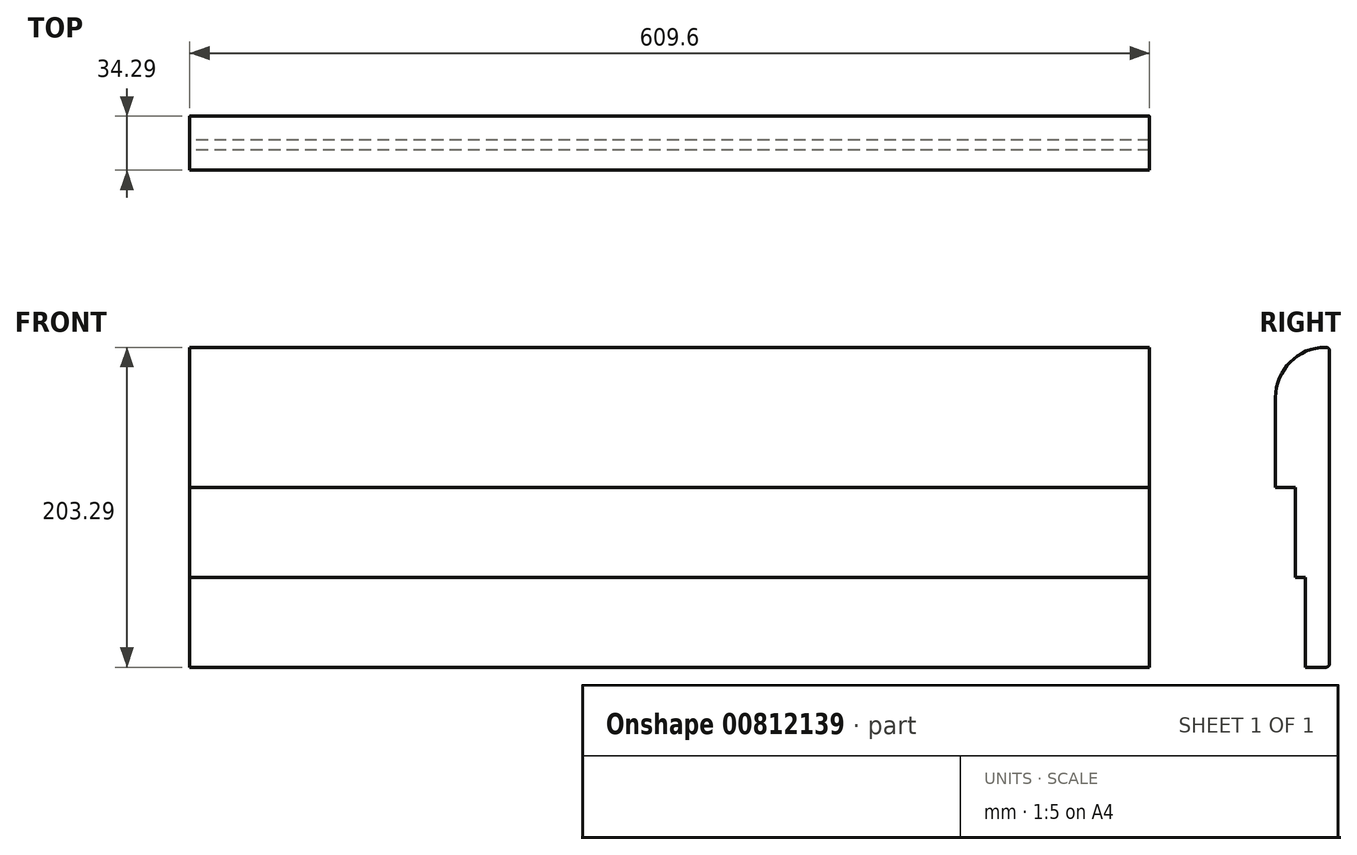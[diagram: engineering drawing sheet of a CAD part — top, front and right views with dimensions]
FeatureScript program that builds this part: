
annotation { "Feature Type Name" : "Feature", "Feature Type Description" : "" }
export const myFeature = defineFeature(function(context is Context, id is Id, definition is map)
    precondition{}
    {
        {
            var Q0;
            Q0=qCreatedBy(makeId("Right.planeOp"),FACE);
            var sketch = newSketch(context, id + "F0", { "sketchPlane" : qUnion([Q0])});
            skLineSegment(sketch, "E0.bottom", {"start": v(-2.54, 0) * mm, "end": v(-15.24, 0) * mm});
            skLineSegment(sketch, "E0.left", {"start": v(0, 2.54) * mm, "end": v(0, 200.75) * mm});
            skLineSegment(sketch, "E0.right", {"start": v(-15.24, 0) * mm, "end": v(-15.24, 57.15) * mm});
            skLineSegment(sketch, "E1", {"start": v(-15.24, 57.15) * mm, "end": v(-21.6, 57.15) * mm});
            skLineSegment(sketch, "E2", {"start": v(-21.6, 57.15) * mm, "end": v(-21.6, 114.3) * mm});
            skLineSegment(sketch, "E3", {"start": v(0, 0) * mm, "end": v(-57.55, 0) * mm, "construction": true});
            skLineSegment(sketch, "E4", {"start": v(-21.6, 114.3) * mm, "end": v(-34.3, 114.3) * mm});
            skLineSegment(sketch, "E5", {"start": v(-34.3, 114.3) * mm, "end": v(-34.3, 171.45) * mm});
            skPoint(sketch, "E6.end.orphan", {"position": v(-34.3, 165.1) * mm});
            skPoint(sketch, "E7.end.orphan", {"position": v(-15.24, 203.2) * mm});
            skPoint(sketch, "E8.orphan", {"position": v(-34.3, 203.2) * mm});
            skArc(sketch, "E9", {"start": v(-2.55, 203.3) * mm, "mid": v(-25, 193.93) * mm, "end": v(-34.29, 171.45) * mm});
            skPoint(sketch, "E10.visualSharp", {"position": v(0, 203.2) * mm});
            skArc(sketch, "E10.filletArc", {"start": v(0, 200.75) * mm, "mid": v(-0.75, 202.55) * mm, "end": v(-2.55, 203.3) * mm});
            skPoint(sketch, "E11.visualSharp", {"position": v(0, 0) * mm});
            skArc(sketch, "E11.filletArc", {"start": v(-2.54, 0) * mm, "mid": v(-0.74, 0.74) * mm, "end": v(0, 2.54) * mm});
            skSolve(sketch);
        }
        {
            var Q0;
            Q0=makeQuery(id+"F0.imprint","IMPRINT",FACE,{"disambiguationData":[TD([[makeQuery(id+"F0.imprint","IMPRINT",EDGE,{"derivedFrom":sQuery(id+"F0.wireOp",EDGE,"E0.bottom")}),-1.0]])]});
            extrude(context, id + "F1", {"entities" : qUnion([Q0]), "depth" : 609.6 * mm, "offsetDistance" : 25.4 * mm});
        }
        {
            var Q0;
            Q0=makeQuery(id+"F1.opExtrude","SWEPT_FACE",FACE,{"disambiguationData":[OSD([sQuery(id+"F0.wireOp",EDGE,"E5")])]});
            cPlane(context, id + "F2", {"entities" : qUnion([Q0]), "cplaneType" : CPlaneType.OFFSET, "offset" : 0 * mm, "width" : 152.4 * mm, "height" : 152.4 * mm});
        }
    });
